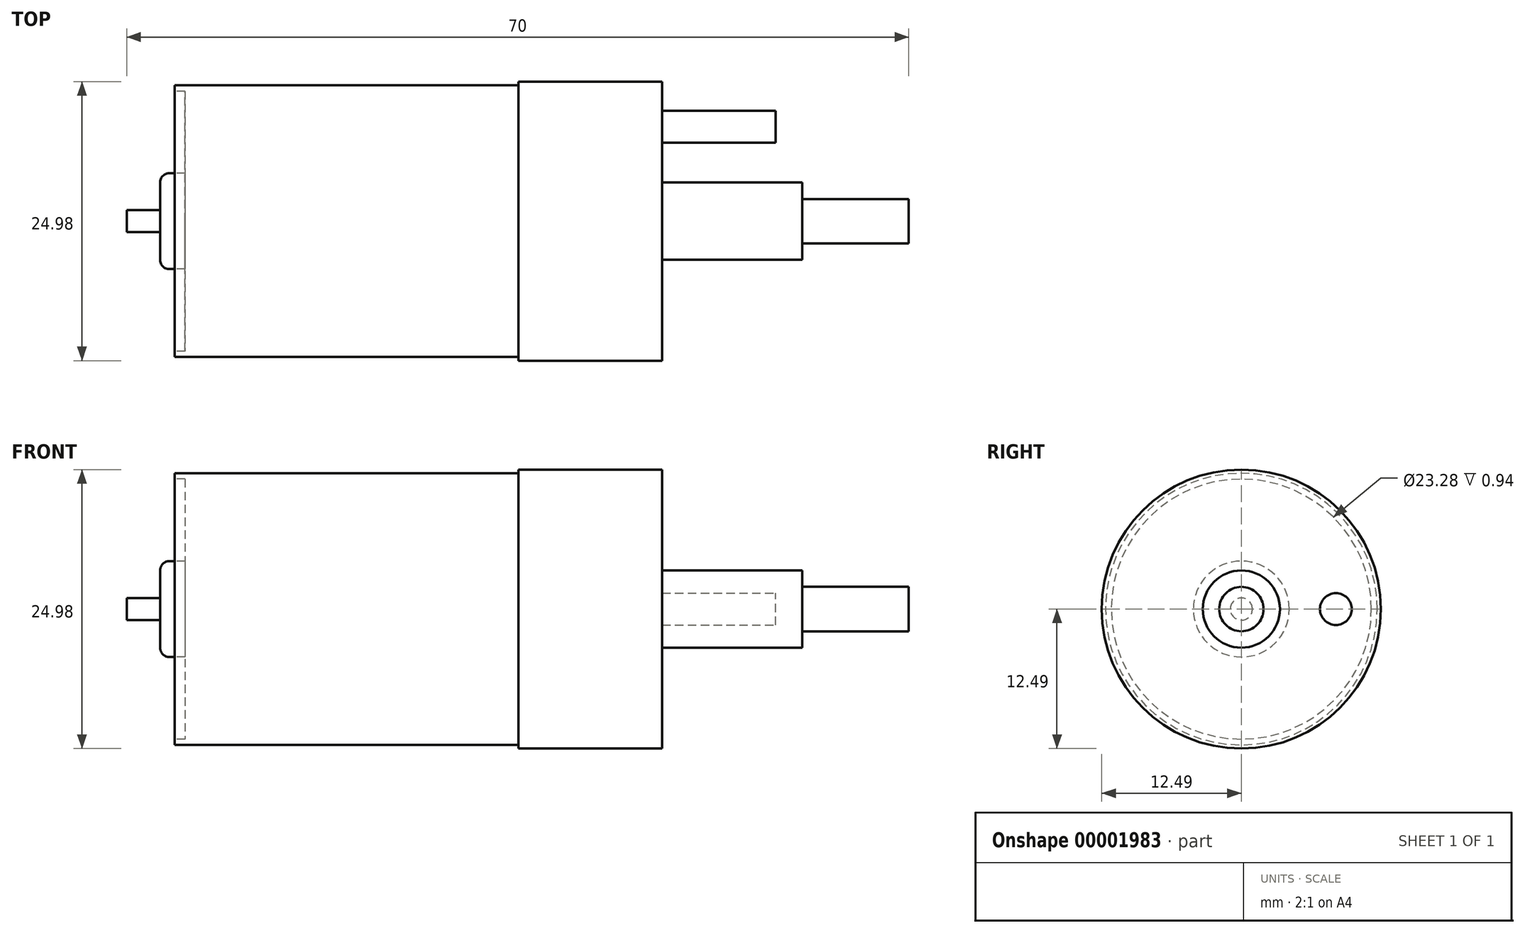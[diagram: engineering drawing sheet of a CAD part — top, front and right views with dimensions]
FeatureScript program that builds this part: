
annotation { "Feature Type Name" : "Feature", "Feature Type Description" : "" }
export const myFeature = defineFeature(function(context is Context, id is Id, definition is map)
    precondition{}
    {
        {
            var Q0;
            Q0=qCreatedBy(makeId("Front.planeOp"),FACE);
            var sketch = newSketch(context, id + "F0", { "sketchPlane" : qUnion([Q0])});
            skLineSegment(sketch, "E0", {"start": v(0, 0) * mm, "end": v(0, 1.98) * mm});
            skLineSegment(sketch, "E1", {"start": v(0, 1.98) * mm, "end": v(-9.53, 1.98) * mm});
            skLineSegment(sketch, "E2", {"start": v(-9.53, 1.98) * mm, "end": v(-9.53, 3.45) * mm});
            skLineSegment(sketch, "E3", {"start": v(-9.53, 3.45) * mm, "end": v(-11.9, 3.45) * mm});
            skLineSegment(sketch, "E4", {"start": v(-11.9, 3.45) * mm, "end": v(-11.9, 12.5) * mm});
            skLineSegment(sketch, "E5", {"start": v(-11.9, 12.5) * mm, "end": v(-34.93, 12.5) * mm});
            skLineSegment(sketch, "E6", {"start": v(-34.93, 12.16) * mm, "end": v(-34.93, 12.5) * mm});
            skLineSegment(sketch, "E7", {"start": v(-34.93, 12.16) * mm, "end": v(-65.7, 12.16) * mm});
            skLineSegment(sketch, "E8", {"start": v(-65.7, 12.16) * mm, "end": v(-65.7, 11.64) * mm});
            skLineSegment(sketch, "E9", {"start": v(-65.7, 11.64) * mm, "end": v(-64.76, 11.64) * mm});
            skLineSegment(sketch, "E10", {"start": v(-64.76, 11.64) * mm, "end": v(-64.76, 4.3) * mm});
            skLineSegment(sketch, "E11", {"start": v(-64.76, 4.3) * mm, "end": v(-66.19, 4.3) * mm});
            skLineSegment(sketch, "E12", {"start": v(-67, 3.48) * mm, "end": v(-67, 1) * mm});
            skLineSegment(sketch, "E13", {"start": v(-67, 1) * mm, "end": v(-70, 1) * mm});
            skLineSegment(sketch, "E14", {"start": v(-70, 1) * mm, "end": v(-70, 0) * mm});
            skLineSegment(sketch, "E15", {"start": v(-70, 0) * mm, "end": v(0, 0) * mm});
            skPoint(sketch, "E16.visualSharp", {"position": v(-67, 4.3) * mm});
            skArc(sketch, "E16.filletArc", {"start": v(-66.19, 4.3) * mm, "mid": v(-66.76, 4.05) * mm, "end": v(-67, 3.48) * mm});
            skSolve(sketch);
        }
        {
            var Q0;
            Q0=makeQuery(id+"F0.imprint","IMPRINT",FACE,{"disambiguationData":[TD([[makeQuery(id+"F0.imprint","IMPRINT",EDGE,{"derivedFrom":sQuery(id+"F0.wireOp",EDGE,"E0")}),1.0]])]});
            var Q1;
            Q1=sQuery(id+"F0.wireOp",EDGE,"E11");
            var Q2;
            Q2=sQuery(id+"F0.wireOp",EDGE,"E4");
            var Q3;
            Q3=sQuery(id+"F0.wireOp",EDGE,"E1");
            var Q4;
            Q4=sQuery(id+"F0.wireOp",EDGE,"E12");
            var Q5;
            Q5=sQuery(id+"F0.wireOp",EDGE,"E13");
            var Q6;
            Q6=sQuery(id+"F0.wireOp",EDGE,"E10");
            var Q7;
            Q7=sQuery(id+"F0.wireOp",EDGE,"E0");
            var Q8;
            Q8=sQuery(id+"F0.wireOp",EDGE,"E7");
            var Q9;
            Q9=sQuery(id+"F0.wireOp",EDGE,"E5");
            var Q10;
            Q10=sQuery(id+"F0.wireOp",EDGE,"E2");
            var Q11;
            Q11=sQuery(id+"F0.wireOp",EDGE,"E3");
            var Q12;
            Q12=sQuery(id+"F0.wireOp",EDGE,"E9");
            var Q13;
            Q13=sQuery(id+"F0.wireOp",EDGE,"E14");
            var Q14;
            Q14=sQuery(id+"F0.wireOp",EDGE,"E8");
            var Q15;
            Q15=sQuery(id+"F0.wireOp",EDGE,"E6");
            var Q16;
            Q16=sQuery(id+"F0.wireOp",EDGE,"E15");
            revolve(context, id + "F1", {"entities" : qUnion([Q0]), "surfaceEntities" : qUnion([Q1, Q2, Q3, Q4, Q5, Q6, Q7, Q8, Q9, Q10, Q11, Q12, Q13, Q14, Q15]), "axis" : qUnion([Q16]), "revolveType" : RevolveType.FULL});
        }
        {
            var Q0;
            Q0=makeQuery(id+"F1.opRevolve","SWEPT_FACE",FACE,{"disambiguationData":[OSD([sQuery(id+"F0.wireOp",EDGE,"E4")])]});
            var sketch = newSketch(context, id + "F2", { "sketchPlane" : qUnion([Q0])});
            skCircle(sketch, "E17", {"center": v(-8.46, 0) * mm, "radius": 1.42 * mm});
            skCircle(sketch, "E18.0.MirrorC", {"center": v(8.46, 0) * mm, "radius": 1.42 * mm});
            skSolve(sketch);
        }
        {
            var Q0;
            Q0=makeQuery(id+"F2.imprint","IMPRINT",FACE,{"disambiguationData":[TD([[makeQuery(id+"F2.imprint","IMPRINT",EDGE,{"derivedFrom":sQuery(id+"F2.wireOp",EDGE,"E17")}),1.0]])]});
            var Q1;
            Q1=makeQuery(id+"F2.imprint","IMPRINT",FACE,{"disambiguationData":[TD([[makeQuery(id+"F2.imprint","IMPRINT",EDGE,{"derivedFrom":sQuery(id+"F2.wireOp",EDGE,"E18.0.MirrorC")}),-1.0]])]});
            extrude(context, id + "F3", {"entities" : qUnion([Q0, Q1]), "operationType" : NewBodyOperationType.REMOVE, "oppositeDirection" : true, "depth" : 10.16 * mm});
        }
    });
